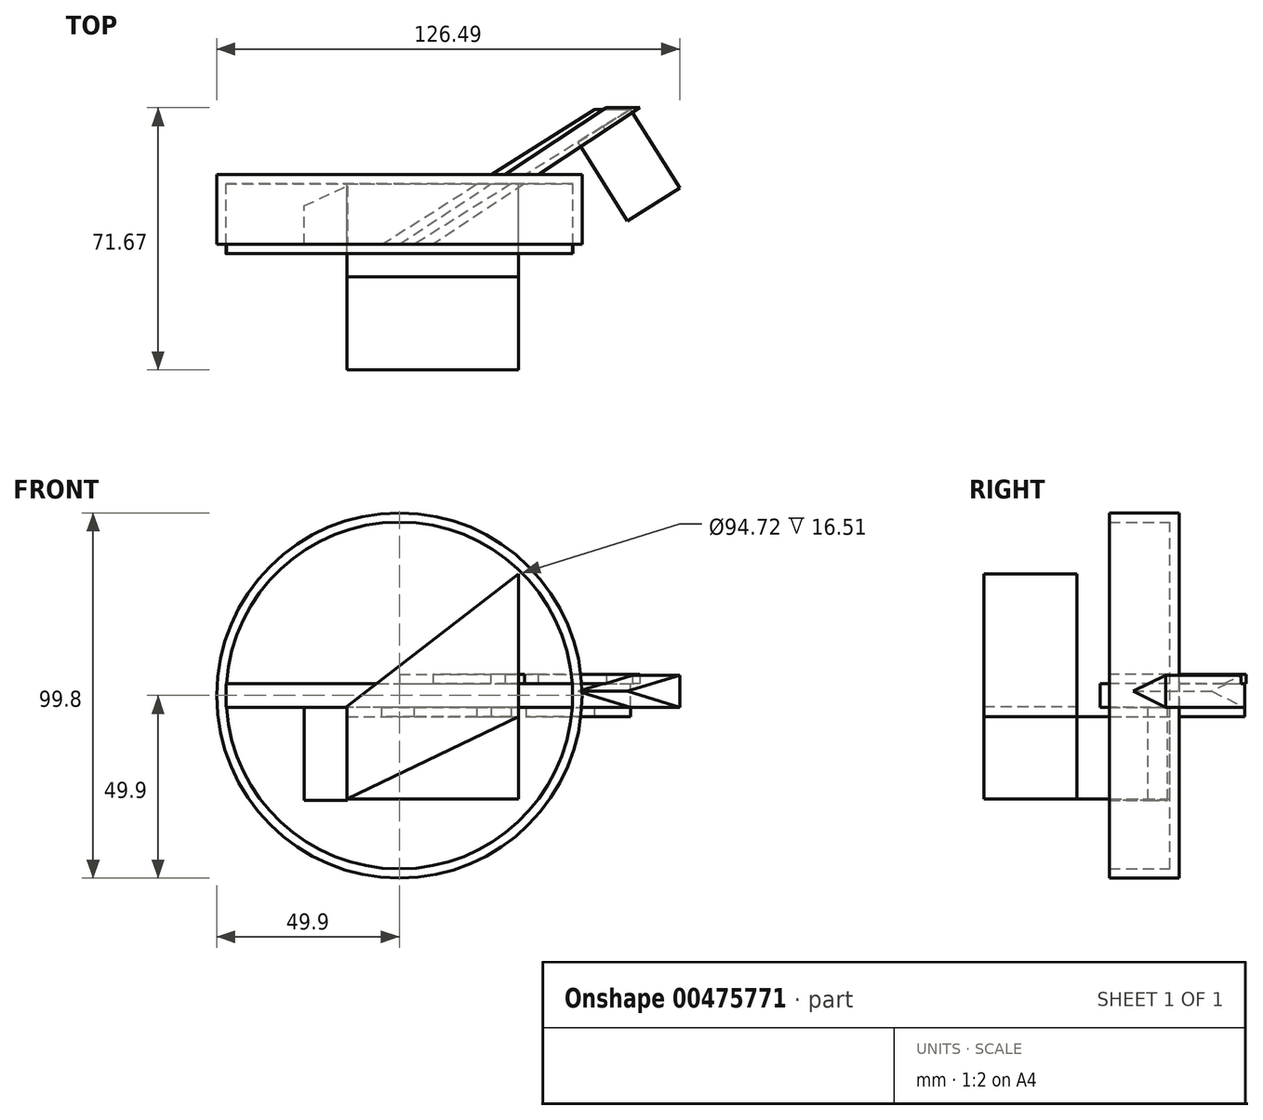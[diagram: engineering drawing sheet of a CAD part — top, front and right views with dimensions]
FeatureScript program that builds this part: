
annotation { "Feature Type Name" : "Feature", "Feature Type Description" : "" }
export const myFeature = defineFeature(function(context is Context, id is Id, definition is map)
    precondition{}
    {
        {
            var Q0;
            Q0=qCreatedBy(makeId("Front.planeOp"),FACE);
            var sketch = newSketch(context, id + "F0", { "sketchPlane" : qUnion([Q0])});
            skCircle(sketch, "E0", {"center": v(0, 0) * mm, "radius": 49.9 * mm});
            skSolve(sketch);
        }
        {
            var Q0;
            Q0=makeQuery(id+"F0.imprint","IMPRINT",FACE,{"disambiguationData":[TD([[makeQuery(id+"F0.imprint","IMPRINT",EDGE,{"derivedFrom":sQuery(id+"F0.wireOp",EDGE,"E0")}),1.0]])]});
            extrude(context, id + "F1", {"entities" : qUnion([Q0]), "depth" : 19.05 * mm});
        }
        {
            var Q0;
            Q0=makeQuery(id+"F1.opExtrude","CAP_FACE",FACE,{"disambiguationData":[OSD([sQuery(id+"F0.wireOp",EDGE,"E0")])],"isStart":false});
            shell(context, id + "F2", {"entities" : qUnion([Q0]), "thickness" : 2.54 * mm});
        }
        {
            var Q0;
            Q0=makeQuery(id+"F1.opExtrude","CAP_FACE",FACE,{"disambiguationData":[OSD([sQuery(id+"F0.wireOp",EDGE,"E0")])],"isStart":false});
            var sketch = newSketch(context, id + "F3", { "sketchPlane" : qUnion([Q0])});
            skLineSegment(sketch, "E1", {"start": v(-49.8, 3.24) * mm, "end": v(49.8, 3.24) * mm});
            skLineSegment(sketch, "E2", {"start": v(49.8, 3.24) * mm, "end": v(49.8, -3.24) * mm});
            skLineSegment(sketch, "E3", {"start": v(49.8, -3.24) * mm, "end": v(-49.8, -3.24) * mm});
            skLineSegment(sketch, "E4", {"start": v(-49.8, -3.24) * mm, "end": v(-49.8, 3.24) * mm});
            skSolve(sketch);
        }
        {
            var Q0;
            {var subQ0=sQuery(id+"F3.wireOp",EDGE,"E1");var subQ1=sQuery(id+"F0.wireOp",EDGE,"E0");var subQ2=makeQuery(id+"F2.opShell","OFFSET_EDGE",EDGE,{"disambiguationData":[OSD([subQ1]),TDD([makeQuery(id+"F1.opExtrude","CAP_EDGE",EDGE,{"disambiguationData":[OSD([subQ1])],"isStart":false})])]});var subQ3=makeQuery(id+"F3.imprint","INTERSECT",VERTEX,{"disambiguationData":[OD(0.0)],"derivedFrom":[subQ2,subQ0]});Q0=makeQuery(id+"F3.imprint","IMPRINT",FACE,{"disambiguationData":[TD([[makeQuery(id+"F3.imprint","IMPRINT",EDGE,{"disambiguationData":[TD([[subQ3,-1.0]])],"derivedFrom":subQ0}),-1.0]])]});}
            extrude(context, id + "F4", {"entities" : qUnion([Q0]), "depth" : 2.54 * mm});
        }
        {
            var Q0;
            Q0=makeQuery(id+"F4.opExtrude","SWEPT_FACE",FACE,{"disambiguationData":[OSD([sQuery(id+"F3.wireOp",EDGE,"E1")])]});
            var sketch = newSketch(context, id + "F5", { "sketchPlane" : qUnion([Q0])});
            skLineSegment(sketch, "E5", {"start": v(0, -19.05) * mm, "end": v(56.54, 18.33) * mm});
            skLineSegment(sketch, "E6", {"start": v(56.54, 18.33) * mm, "end": v(65.76, 18.33) * mm});
            skLineSegment(sketch, "E7", {"start": v(65.76, 18.33) * mm, "end": v(9.22, -19.05) * mm});
            skLineSegment(sketch, "E8", {"start": v(9.22, -19.05) * mm, "end": v(0, -19.05) * mm});
            skSolve(sketch);
        }
        {
            var Q0;
            Q0=makeQuery(id+"F5.imprint","IMPRINT",FACE,{"disambiguationData":[TD([[makeQuery(id+"F5.imprint","IMPRINT",EDGE,{"derivedFrom":sQuery(id+"F5.wireOp",EDGE,"E5")}),-1.0]])]});
            extrude(context, id + "F6", {"entities" : qUnion([Q0]), "operationType" : NewBodyOperationType.ADD, "depth" : 2.54 * mm});
        }
        {
            var Q0;
            Q0=makeQuery(id+"F4.opExtrude","SWEPT_FACE",FACE,{"disambiguationData":[OSD([sQuery(id+"F3.wireOp",EDGE,"E3")])]});
            var sketch = newSketch(context, id + "F7", { "sketchPlane" : qUnion([Q0])});
            skLineSegment(sketch, "E9", {"start": v(-8.8, 21.59) * mm, "end": v(53.4, -17.88) * mm});
            skLineSegment(sketch, "E10", {"start": v(53.4, -17.88) * mm, "end": v(63.12, -17.88) * mm});
            skLineSegment(sketch, "E11", {"start": v(63.12, -17.88) * mm, "end": v(0, 21.6) * mm});
            skLineSegment(sketch, "E12", {"start": v(0, 21.6) * mm, "end": v(-8.8, 21.59) * mm});
            skSolve(sketch);
        }
        {
            var Q0;
            {var subQ0=sQuery(id+"F7.wireOp",EDGE,"E10");Q0=makeQuery(id+"F7.imprint","IMPRINT",FACE,{"disambiguationData":[TD([[makeQuery(id+"F7.imprint","IMPRINT",EDGE,{"derivedFrom":subQ0}),1.0]])]});}
            extrude(context, id + "F8", {"entities" : qUnion([Q0]), "operationType" : NewBodyOperationType.ADD, "depth" : 2.54 * mm});
        }
        {
            var Q0;
            {var subQ0=sQuery(id+"F7.wireOp",EDGE,"E11");Q0=makeQuery(id+"F8.boolean.opBoolean","SPLIT",FACE,{"disambiguationData":[TD([makeQuery(id+"F1.opExtrude","CAP_FACE",FACE,{"disambiguationData":[OSD([sQuery(id+"F0.wireOp",EDGE,"E0")])],"isStart":true})])],"derivedFrom":makeQuery(id+"F8.opExtrude","SWEPT_FACE",FACE,{"disambiguationData":[OSD([subQ0])]})});}
            var sketch = newSketch(context, id + "F9", { "sketchPlane" : qUnion([Q0])});
            skLineSegment(sketch, "E13", {"start": v(63, -3.24) * mm, "end": v(63, 5.52) * mm});
            skLineSegment(sketch, "E14", {"start": v(63, 5.52) * mm, "end": v(29.28, -3.24) * mm});
            skLineSegment(sketch, "E15", {"start": v(29.28, -3.24) * mm, "end": v(29.28, 5.52) * mm});
            skLineSegment(sketch, "E16", {"start": v(29.28, 5.52) * mm, "end": v(63, -3.24) * mm});
            skSolve(sketch);
        }
        {
            var Q0;
            {var subQ0=sQuery(id+"F9.wireOp",EDGE,"E13");Q0=makeQuery(id+"F9.imprint","IMPRINT",FACE,{"disambiguationData":[TD([[makeQuery(id+"F9.imprint","IMPRINT",EDGE,{"derivedFrom":subQ0}),1.0]])]});}
            extrude(context, id + "F10", {"entities" : qUnion([Q0]), "operationType" : NewBodyOperationType.ADD, "depth" : 25.4 * mm});
        }
        {
            var Q0;
            Q0=makeQuery(id+"F4.opExtrude","SWEPT_FACE",FACE,{"disambiguationData":[OSD([sQuery(id+"F3.wireOp",EDGE,"E3")])]});
            var sketch = newSketch(context, id + "F11", { "sketchPlane" : qUnion([Q0])});
            skLineSegment(sketch, "E17", {"start": v(-26, 21.59) * mm, "end": v(-26, 8.5) * mm});
            skLineSegment(sketch, "E18", {"start": v(-26, 8.5) * mm, "end": v(-14.23, 3.1) * mm});
            skLineSegment(sketch, "E19", {"start": v(-14.23, 3.1) * mm, "end": v(-14.23, 19.05) * mm});
            skLineSegment(sketch, "E20", {"start": v(-14.23, 19.05) * mm, "end": v(-26, 21.59) * mm});
            skSolve(sketch);
        }
        {
            var Q0;
            {var subQ0=sQuery(id+"F11.wireOp",EDGE,"E18");Q0=makeQuery(id+"F11.imprint","IMPRINT",FACE,{"disambiguationData":[TD([[makeQuery(id+"F11.imprint","IMPRINT",EDGE,{"derivedFrom":subQ0}),1.0]])]});}
            extrude(context, id + "F12", {"entities" : qUnion([Q0]), "depth" : 25.4 * mm});
        }
        {
            var Q0;
            {var subQ0=sQuery(id+"F0.wireOp",EDGE,"E0");Q0=makeQuery(id+"F2.opShell","OFFSET_FACE",FACE,{"disambiguationData":[OSD([subQ0]),TDD([makeQuery(id+"F1.opExtrude","CAP_FACE",FACE,{"disambiguationData":[OSD([subQ0])],"isStart":true})])]});}
            var sketch = newSketch(context, id + "F13", { "sketchPlane" : qUnion([Q0])});
            skLineSegment(sketch, "E21.bottom", {"start": v(-14.29, -28.2) * mm, "end": v(32.58, -28.2) * mm});
            skLineSegment(sketch, "E21.top", {"start": v(-14.29, -5.78) * mm, "end": v(32.58, -5.78) * mm});
            skLineSegment(sketch, "E21.left", {"start": v(-14.29, -28.2) * mm, "end": v(-14.29, -5.78) * mm});
            skLineSegment(sketch, "E21.right", {"start": v(32.58, -28.2) * mm, "end": v(32.58, -5.78) * mm});
            skSolve(sketch);
        }
        {
            var Q0;
            Q0=makeQuery(id+"F13.imprint","IMPRINT",FACE,{"disambiguationData":[TD([[makeQuery(id+"F13.imprint","IMPRINT",EDGE,{"derivedFrom":sQuery(id+"F13.wireOp",EDGE,"E21.bottom")}),1.0]])]});
            extrude(context, id + "F14", {"entities" : qUnion([Q0]), "depth" : 25.4 * mm});
        }
        {
            var Q0;
            Q0=makeQuery(id+"F14.opExtrude","CAP_FACE",FACE,{"disambiguationData":[OSD([sQuery(id+"F13.wireOp",EDGE,"E21.bottom"),sQuery(id+"F13.wireOp",EDGE,"E21.top"),sQuery(id+"F13.wireOp",EDGE,"E21.left"),sQuery(id+"F13.wireOp",EDGE,"E21.right")])],"isStart":false});
            var sketch = newSketch(context, id + "F15", { "sketchPlane" : qUnion([Q0])});
            skLineSegment(sketch, "E22", {"start": v(-14.29, -28.2) * mm, "end": v(-14.29, -3.05) * mm});
            skLineSegment(sketch, "E23", {"start": v(-14.29, -3.05) * mm, "end": v(32.58, 33.15) * mm});
            skLineSegment(sketch, "E24", {"start": v(32.58, 33.15) * mm, "end": v(32.58, -5.78) * mm});
            skLineSegment(sketch, "E25", {"start": v(32.58, -5.78) * mm, "end": v(-14.29, -28.2) * mm});
            skSolve(sketch);
        }
        {
            var Q0;
            {var subQ0=sQuery(id+"F15.wireOp",EDGE,"E25");Q0=makeQuery(id+"F15.imprint","IMPRINT",FACE,{"disambiguationData":[TD([[makeQuery(id+"F15.imprint","IMPRINT",EDGE,{"derivedFrom":subQ0}),-1.0]])]});}
            var Q1;
            {var subQ2=sQuery(id+"F15.wireOp",EDGE,"E23");Q1=makeQuery(id+"F15.imprint","IMPRINT",FACE,{"disambiguationData":[TD([[makeQuery(id+"F15.imprint","IMPRINT",EDGE,{"derivedFrom":subQ2}),-1.0]])]});}
            extrude(context, id + "F16", {"entities" : qUnion([Q0, Q1]), "operationType" : NewBodyOperationType.ADD, "depth" : 25.4 * mm});
        }
    });
